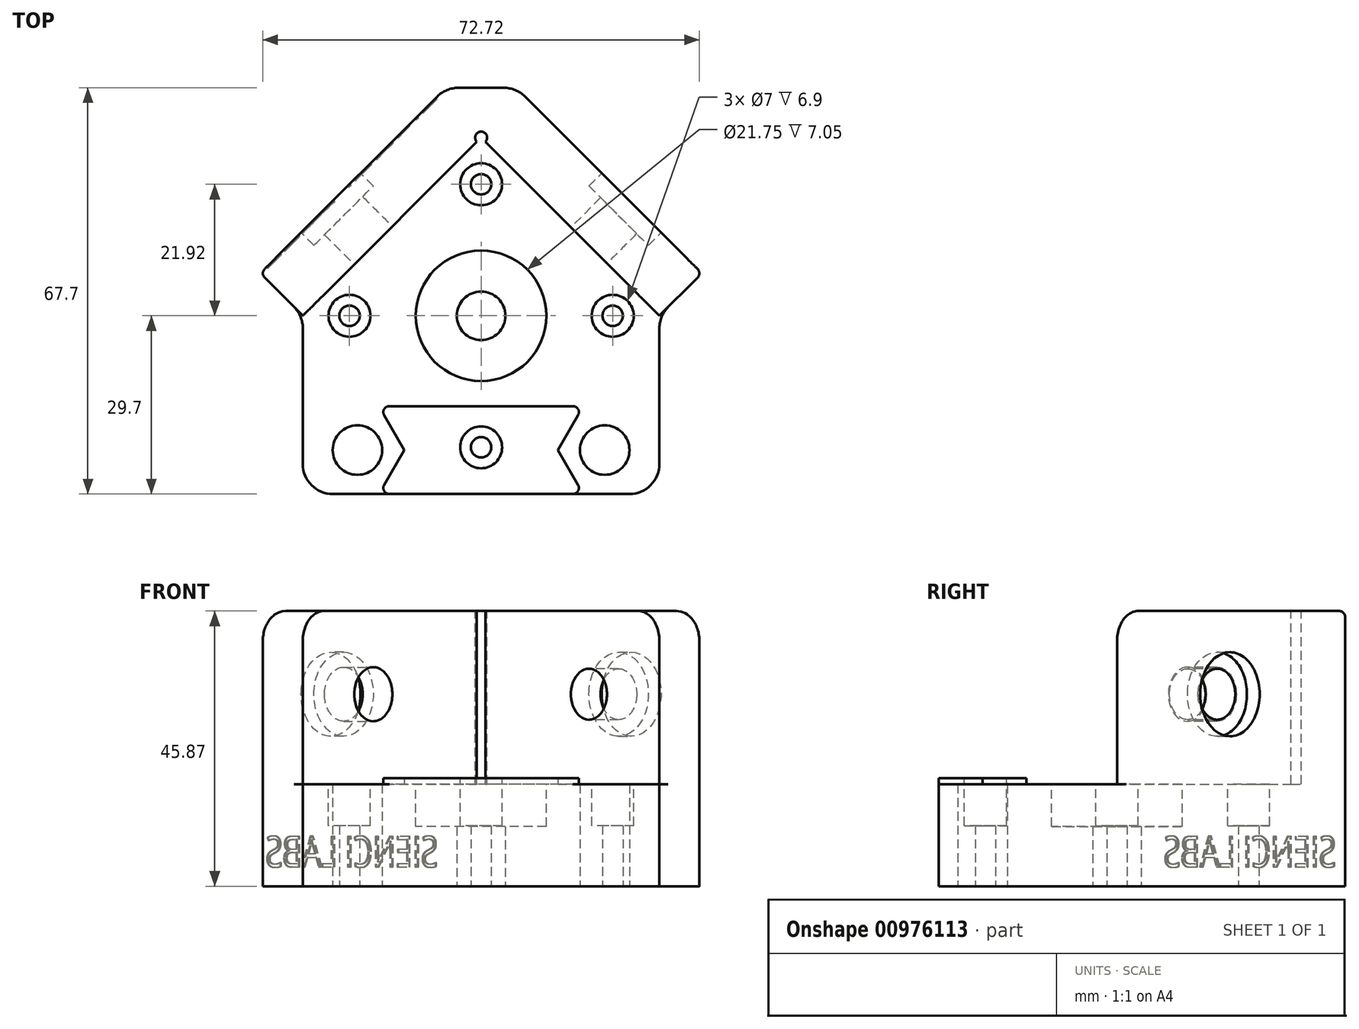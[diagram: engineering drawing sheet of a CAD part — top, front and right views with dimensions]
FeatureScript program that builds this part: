
annotation { "Feature Type Name" : "Feature", "Feature Type Description" : "" }
export const myFeature = defineFeature(function(context is Context, id is Id, definition is map)
    precondition{}
    {
        {
            var Q0;
            Q0=qCreatedBy(makeId("Top.planeOp"),FACE);
            var sketch = newSketch(context, id + "F0", { "sketchPlane" : qUnion([Q0])});
            skLineSegment(sketch, "E0", {"start": v(0, 0) * mm, "end": v(-29.7, 0) * mm});
            skLineSegment(sketch, "E1", {"start": v(-29.7, 0) * mm, "end": v(-29.7, 29.7) * mm});
            skLineSegment(sketch, "E2", {"start": v(-29.7, 29.7) * mm, "end": v(0, 59.4) * mm});
            skLineSegment(sketch, "E3", {"start": v(0, 59.4) * mm, "end": v(0, 0) * mm, "construction": true});
            skLineSegment(sketch, "E4", {"start": v(-29.7, 7.78) * mm, "end": v(0, 7.78) * mm, "construction": true});
            skCircle(sketch, "E5", {"center": v(0, 29.7) * mm, "radius": 4.05 * mm});
            skLineSegment(sketch, "E6", {"start": v(0, 29.7) * mm, "end": v(0, 59.4) * mm, "construction": true});
            skLineSegment(sketch, "E7", {"start": v(0, 59.4) * mm, "end": v(-29.7, 29.7) * mm, "construction": true});
            skLineSegment(sketch, "E8", {"start": v(-29.7, 29.7) * mm, "end": v(0, 0) * mm, "construction": true});
            skLineSegment(sketch, "E9", {"start": v(0, 51.62) * mm, "end": v(-21.92, 29.7) * mm, "construction": true});
            skLineSegment(sketch, "E10", {"start": v(-21.92, 29.7) * mm, "end": v(0, 7.78) * mm, "construction": true});
            skCircle(sketch, "E11", {"center": v(-20.59, 7.32) * mm, "radius": 4.12 * mm});
            skCircle(sketch, "E12", {"center": v(-21.92, 29.7) * mm, "radius": 1.7 * mm});
            skCircle(sketch, "E13", {"center": v(0, 51.62) * mm, "radius": 1.7 * mm});
            skCircle(sketch, "E14", {"center": v(0, 7.78) * mm, "radius": 1.7 * mm});
            skLineSegment(sketch, "E15.MirrorCS", {"start": v(29.7, 29.7) * mm, "end": v(0, 59.4) * mm});
            skLineSegment(sketch, "E16.MirrorCS", {"start": v(0, 0) * mm, "end": v(29.7, 0) * mm});
            skLineSegment(sketch, "E17.MirrorCS", {"start": v(29.7, 0) * mm, "end": v(29.7, 29.7) * mm});
            skLineSegment(sketch, "E18.MirrorCS", {"start": v(29.7, 7.78) * mm, "end": v(0, 7.78) * mm, "construction": true});
            skCircle(sketch, "E19.MirrorC", {"center": v(21.92, 29.7) * mm, "radius": 1.7 * mm});
            skCircle(sketch, "E20.MirrorC", {"center": v(20.6, 7.32) * mm, "radius": 4.12 * mm});
            skLineSegment(sketch, "E21.MirrorCS", {"start": v(0, 59.4) * mm, "end": v(29.7, 29.7) * mm, "construction": true});
            skLineSegment(sketch, "E22.MirrorCS", {"start": v(0, 51.62) * mm, "end": v(21.92, 29.7) * mm, "construction": true});
            skLineSegment(sketch, "E23.MirrorCS", {"start": v(21.92, 29.7) * mm, "end": v(0, 7.78) * mm, "construction": true});
            skLineSegment(sketch, "E24.MirrorCS", {"start": v(29.7, 29.7) * mm, "end": v(0, 0) * mm, "construction": true});
            skSolve(sketch);
        }
        {
            var Q0;
            Q0=qSketchRegion(id+"F0",true);
            extrude(context, id + "F1", {"entities" : qUnion([Q0]), "depth" : 13 * mm, "offsetDistance" : 25 * mm});
        }
        {
            var Q0;
            Q0=makeQuery(id+"F1.opExtrude","CAP_FACE",FACE,{"disambiguationData":[OSD([sQuery(id+"F0.wireOp",EDGE,"E0"),sQuery(id+"F0.wireOp",EDGE,"E1"),sQuery(id+"F0.wireOp",EDGE,"E2"),sQuery(id+"F0.wireOp",EDGE,"E5"),sQuery(id+"F0.wireOp",EDGE,"E11"),sQuery(id+"F0.wireOp",EDGE,"E12"),sQuery(id+"F0.wireOp",EDGE,"E15.MirrorCS"),sQuery(id+"F0.wireOp",EDGE,"E16.MirrorCS"),sQuery(id+"F0.wireOp",EDGE,"E17.MirrorCS"),sQuery(id+"F0.wireOp",EDGE,"E14"),sQuery(id+"F0.wireOp",EDGE,"E13"),sQuery(id+"F0.wireOp",EDGE,"E19.MirrorC"),sQuery(id+"F0.wireOp",EDGE,"E20.MirrorC")])],"isStart":true});
            var sketch = newSketch(context, id + "F2", { "sketchPlane" : qUnion([Q0])});
            skLineSegment(sketch, "E25", {"start": v(-29.7, -29.7) * mm, "end": v(-36.77, -36.77) * mm});
            skLineSegment(sketch, "E26", {"start": v(-36.77, -36.77) * mm, "end": v(-5.84, -67.7) * mm});
            skLineSegment(sketch, "E27", {"start": v(-5.84, -67.7) * mm, "end": v(0, -67.7) * mm});
            skLineSegment(sketch, "E28", {"start": v(0, -29.7) * mm, "end": v(-4.05, -29.7) * mm, "construction": true});
            skLineSegment(sketch, "E29", {"start": v(0, -67.7) * mm, "end": v(0, -29.7) * mm, "construction": true});
            skLineSegment(sketch, "E30.MirrorCS", {"start": v(0, -29.7) * mm, "end": v(4.05, -29.7) * mm, "construction": true});
            skLineSegment(sketch, "E31.MirrorCS", {"start": v(5.84, -67.7) * mm, "end": v(0, -67.7) * mm});
            skLineSegment(sketch, "E32.MirrorCS", {"start": v(36.77, -36.77) * mm, "end": v(5.84, -67.7) * mm});
            skLineSegment(sketch, "E33.MirrorCS", {"start": v(29.7, -29.7) * mm, "end": v(36.77, -36.77) * mm});
            skLineSegment(sketch, "E34", {"start": v(-29.7, -29.7) * mm, "end": v(0, -59.4) * mm});
            skLineSegment(sketch, "E35", {"start": v(0, -59.4) * mm, "end": v(29.7, -29.7) * mm});
            skSolve(sketch);
        }
        {
            var Q0;
            Q0=qSketchRegion(id+"F2",true);
            var Q1;
            Q1=qSketchRegion(id+"F6",true);
            extrude(context, id + "F3", {"entities" : qUnion([Q0, Q1]), "operationType" : NewBodyOperationType.ADD, "oppositeDirection" : true, "depth" : 45.87 * mm, "offsetDistance" : 25 * mm});
        }
        {
            var Q0;
            Q0=makeQuery(id+"F3.opExtrude","SWEPT_FACE",FACE,{"disambiguationData":[OSD([sQuery(id+"F2.wireOp",EDGE,"E34")])]});
            var sketch = newSketch(context, id + "F4", { "sketchPlane" : qUnion([Q0])});
            skCircle(sketch, "E36", {"center": v(16.6, 32) * mm, "radius": 4.5 * mm});
            skLineSegment(sketch, "E37", {"start": v(42, 13) * mm, "end": v(-8.8, 13) * mm, "construction": true});
            skLineSegment(sketch, "E38", {"start": v(16.6, 13) * mm, "end": v(16.6, 45.87) * mm, "construction": true});
            skSolve(sketch);
        }
        {
            var Q0;
            Q0=qSketchRegion(id+"F4",true);
            extrude(context, id + "F5", {"entities" : qUnion([Q0]), "operationType" : NewBodyOperationType.REMOVE, "endBound" : BoundingType.UP_TO_NEXT, "oppositeDirection" : true, "depth" : 25 * mm, "offsetDistance" : 25 * mm});
        }
        {
            var Q0;
            Q0=makeQuery(id+"F3.opExtrude","SWEPT_FACE",FACE,{"disambiguationData":[OSD([sQuery(id+"F2.wireOp",EDGE,"E35")])]});
            var sketch = newSketch(context, id + "F6", { "sketchPlane" : qUnion([Q0])});
            skLineSegment(sketch, "E39", {"start": v(-42, 13) * mm, "end": v(8.8, 13) * mm, "construction": true});
            skLineSegment(sketch, "E40", {"start": v(-16.6, 13) * mm, "end": v(-16.6, 45.87) * mm, "construction": true});
            skCircle(sketch, "E41", {"center": v(-16.6, 32) * mm, "radius": 4.25 * mm});
            skSolve(sketch);
        }
        {
            var Q0;
            Q0=qSketchRegion(id+"F6",true);
            extrude(context, id + "F7", {"entities" : qUnion([Q0]), "operationType" : NewBodyOperationType.REMOVE, "endBound" : BoundingType.UP_TO_NEXT, "oppositeDirection" : true, "depth" : 25 * mm, "offsetDistance" : 25 * mm});
        }
        {
            var Q0;
            Q0=makeQuery(id+"F3.opExtrude","SWEPT_FACE",FACE,{"disambiguationData":[OSD([sQuery(id+"F2.wireOp",EDGE,"E26")])]});
            var sketch = newSketch(context, id + "F8", { "sketchPlane" : qUnion([Q0])});
            skCircle(sketch, "E42", {"center": v(-16.6, 32) * mm, "radius": 7 * mm});
            skSolve(sketch);
        }
        {
            var Q0;
            Q0=qSketchRegion(id+"F8",true);
            extrude(context, id + "F9", {"entities" : qUnion([Q0]), "operationType" : NewBodyOperationType.REMOVE, "oppositeDirection" : true, "depth" : 3 * mm, "offsetDistance" : 25 * mm});
        }
        {
            var Q0;
            Q0=makeQuery(id+"F3.opExtrude","SWEPT_FACE",FACE,{"disambiguationData":[OSD([sQuery(id+"F2.wireOp",EDGE,"E32.MirrorCS")])]});
            var sketch = newSketch(context, id + "F10", { "sketchPlane" : qUnion([Q0])});
            skCircle(sketch, "E43", {"center": v(16.6, 32) * mm, "radius": 7 * mm});
            skSolve(sketch);
        }
        {
            var Q0;
            Q0=qSketchRegion(id+"F10",true);
            extrude(context, id + "F11", {"entities" : qUnion([Q0]), "operationType" : NewBodyOperationType.REMOVE, "oppositeDirection" : true, "depth" : 3 * mm, "offsetDistance" : 25 * mm});
        }
        {
            var Q0;
            Q0=makeQuery(id+"F1.opExtrude","CAP_FACE",FACE,{"disambiguationData":[OSD([sQuery(id+"F0.wireOp",EDGE,"E0"),sQuery(id+"F0.wireOp",EDGE,"E1"),sQuery(id+"F0.wireOp",EDGE,"E2"),sQuery(id+"F0.wireOp",EDGE,"E5"),sQuery(id+"F0.wireOp",EDGE,"E11"),sQuery(id+"F0.wireOp",EDGE,"E12"),sQuery(id+"F0.wireOp",EDGE,"E15.MirrorCS"),sQuery(id+"F0.wireOp",EDGE,"E16.MirrorCS"),sQuery(id+"F0.wireOp",EDGE,"E17.MirrorCS"),sQuery(id+"F0.wireOp",EDGE,"E14"),sQuery(id+"F0.wireOp",EDGE,"E13"),sQuery(id+"F0.wireOp",EDGE,"E19.MirrorC"),sQuery(id+"F0.wireOp",EDGE,"E20.MirrorC")])],"isStart":false});
            var sketch = newSketch(context, id + "F12", { "sketchPlane" : qUnion([Q0])});
            skCircle(sketch, "E44", {"center": v(0, 51.62) * mm, "radius": 3.5 * mm});
            skCircle(sketch, "E45", {"center": v(-21.92, 29.7) * mm, "radius": 3.5 * mm});
            skCircle(sketch, "E46", {"center": v(21.92, 29.7) * mm, "radius": 3.5 * mm});
            skCircle(sketch, "E47", {"center": v(0, 7.78) * mm, "radius": 3.5 * mm});
            skSolve(sketch);
        }
        {
            var Q0;
            Q0=makeQuery(id+"F3.opExtrude","CAP_EDGE",EDGE,{"disambiguationData":[OSD([sQuery(id+"F2.wireOp",EDGE,"E33.MirrorCS")])],"isStart":false});
            var Q1;
            Q1=makeQuery(id+"F3.opExtrude","CAP_EDGE",EDGE,{"disambiguationData":[OSD([sQuery(id+"F2.wireOp",EDGE,"E25")])],"isStart":false});
            var Q2;
            {var subQ0=sQuery(id+"F0.wireOp",EDGE,"E17.MirrorCS");Q2=makeQuery(id+"F3.boolean.opBoolean","MERGE",EDGE,{"derivedFrom":[makeQuery(id+"F1.opExtrude","SWEPT_EDGE",EDGE,{"disambiguationData":[OSD([sQuery(id+"F0.wireOp",EDGE,"E15.MirrorCS"),subQ0])]}),makeQuery(id+"F3.opExtrude","SWEPT_EDGE",EDGE,{"disambiguationData":[OSD([subQ0,sQuery(id+"F2.wireOp",EDGE,"E33.MirrorCS"),sQuery(id+"F2.wireOp",EDGE,"E35")])]})]});}
            var Q3;
            Q3=makeQuery(id+"F1.opExtrude","SWEPT_EDGE",EDGE,{"disambiguationData":[OSD([sQuery(id+"F0.wireOp",EDGE,"E16.MirrorCS"),sQuery(id+"F0.wireOp",EDGE,"E17.MirrorCS")])]});
            var Q4;
            Q4=makeQuery(id+"F1.opExtrude","SWEPT_EDGE",EDGE,{"disambiguationData":[OSD([sQuery(id+"F0.wireOp",EDGE,"E0"),sQuery(id+"F0.wireOp",EDGE,"E1")])]});
            var Q5;
            {var subQ0=sQuery(id+"F0.wireOp",EDGE,"E1");Q5=makeQuery(id+"F3.boolean.opBoolean","MERGE",EDGE,{"derivedFrom":[makeQuery(id+"F1.opExtrude","SWEPT_EDGE",EDGE,{"disambiguationData":[OSD([subQ0,sQuery(id+"F0.wireOp",EDGE,"E2")])]}),makeQuery(id+"F3.opExtrude","SWEPT_EDGE",EDGE,{"disambiguationData":[OSD([subQ0,sQuery(id+"F2.wireOp",EDGE,"E25"),sQuery(id+"F2.wireOp",EDGE,"E34")])]})]});}
            var Q6;
            Q6=makeQuery(id+"F3.opExtrude","SWEPT_EDGE",EDGE,{"disambiguationData":[OSD([sQuery(id+"F2.wireOp",EDGE,"E26"),sQuery(id+"F2.wireOp",EDGE,"E27")])]});
            var Q7;
            Q7=makeQuery(id+"F3.opExtrude","SWEPT_EDGE",EDGE,{"disambiguationData":[OSD([sQuery(id+"F2.wireOp",EDGE,"E31.MirrorCS"),sQuery(id+"F2.wireOp",EDGE,"E32.MirrorCS")])]});
            fillet(context, id + "F13", {"entities" : qUnion([Q0, Q1, Q2, Q3, Q4, Q5, Q6, Q7]), "radius" : 5 * mm, "tangentPropagation" : true, "allowEdgeOverflow" : false});
        }
        {
            var Q0;
            Q0=qSketchRegion(id+"F12",true);
            extrude(context, id + "F14", {"entities" : qUnion([Q0]), "operationType" : NewBodyOperationType.REMOVE, "oppositeDirection" : true, "depth" : 2.9 * mm, "offsetDistance" : 25 * mm});
        }
        {
            var Q0;
            Q0=makeQuery(id+"F3.opExtrude","SWEPT_FACE",FACE,{"disambiguationData":[OSD([sQuery(id+"F2.wireOp",EDGE,"E26")])]});
            var sketch = newSketch(context, id + "F15", { "sketchPlane" : qUnion([Q0])});
            skText(sketch, "E48", { "text": "SIENCI LABS\n", "fontName": "OpenSans-Regular.ttf"});
            const initialGuessF15  = {"E48": [-0.04167, 0.0032, 1, 0, 0.00516]};
            skSetInitialGuess(sketch, initialGuessF15);
            skSolve(sketch);
        }
        {
            var Q0;
            Q0=qSketchRegion(id+"F15",true);
            extrude(context, id + "F16", {"entities" : qUnion([Q0]), "operationType" : NewBodyOperationType.REMOVE, "oppositeDirection" : true, "depth" : 0.25 * mm, "offsetDistance" : 25 * mm});
        }
        {
            var Q0;
            Q0=makeQuery(id+"F1.opExtrude","CAP_FACE",FACE,{"disambiguationData":[OSD([sQuery(id+"F0.wireOp",EDGE,"E0"),sQuery(id+"F0.wireOp",EDGE,"E1"),sQuery(id+"F0.wireOp",EDGE,"E2"),sQuery(id+"F0.wireOp",EDGE,"E5"),sQuery(id+"F0.wireOp",EDGE,"E11"),sQuery(id+"F0.wireOp",EDGE,"E12"),sQuery(id+"F0.wireOp",EDGE,"E15.MirrorCS"),sQuery(id+"F0.wireOp",EDGE,"E16.MirrorCS"),sQuery(id+"F0.wireOp",EDGE,"E17.MirrorCS"),sQuery(id+"F0.wireOp",EDGE,"E14"),sQuery(id+"F0.wireOp",EDGE,"E13"),sQuery(id+"F0.wireOp",EDGE,"E19.MirrorC"),sQuery(id+"F0.wireOp",EDGE,"E20.MirrorC")])],"isStart":false});
            var sketch = newSketch(context, id + "F17", { "sketchPlane" : qUnion([Q0])});
            skCircle(sketch, "E49.cCircle", {"center": v(-20.59, 7.32) * mm, "radius": 6.75 * mm, "construction": true});
            skLineSegment(sketch, "E49.0", {"start": v(-16.7, 14.07) * mm, "end": v(-12.8, 7.32) * mm});
            skLineSegment(sketch, "E49.1", {"start": v(-12.8, 7.32) * mm, "end": v(-16.7, 0.57) * mm});
            skLineSegment(sketch, "E49.2", {"start": v(-16.7, 0.57) * mm, "end": v(-24.49, 0.57) * mm});
            skLineSegment(sketch, "E49.3", {"start": v(-24.49, 0.57) * mm, "end": v(-28.38, 7.32) * mm});
            skLineSegment(sketch, "E49.4", {"start": v(-28.38, 7.32) * mm, "end": v(-24.49, 14.07) * mm});
            skLineSegment(sketch, "E49.5", {"start": v(-24.49, 14.07) * mm, "end": v(-16.7, 14.07) * mm});
            skPoint(sketch, "E49.0.midPoint", {"position": v(-14.74, 10.7) * mm});
            skLineSegment(sketch, "E50", {"start": v(0, 59.4) * mm, "end": v(0, 0) * mm, "construction": true});
            skLineSegment(sketch, "E51.MirrorCS", {"start": v(24.49, 14.07) * mm, "end": v(16.7, 14.07) * mm});
            skLineSegment(sketch, "E52.MirrorCS", {"start": v(16.7, 14.07) * mm, "end": v(12.8, 7.32) * mm});
            skLineSegment(sketch, "E53.MirrorCS", {"start": v(28.38, 7.32) * mm, "end": v(24.49, 14.07) * mm});
            skCircle(sketch, "E54.MirrorC", {"center": v(20.59, 7.32) * mm, "radius": 6.75 * mm, "construction": true});
            skLineSegment(sketch, "E55.MirrorCS", {"start": v(24.49, 0.57) * mm, "end": v(28.38, 7.32) * mm});
            skLineSegment(sketch, "E56.MirrorCS", {"start": v(12.8, 7.32) * mm, "end": v(16.7, 0.57) * mm});
            skLineSegment(sketch, "E57.MirrorCS", {"start": v(16.7, 0.57) * mm, "end": v(24.49, 0.57) * mm});
            skPoint(sketch, "E58.MirrorP", {"position": v(14.74, 10.7) * mm});
            skLineSegment(sketch, "E59", {"start": v(-16.7, 14.07) * mm, "end": v(16.7, 14.07) * mm});
            skLineSegment(sketch, "E60", {"start": v(-16.7, 0.57) * mm, "end": v(16.7, 0.57) * mm});
            skCircle(sketch, "E61", {"center": v(0, 7.78) * mm, "radius": 3.5 * mm});
            skLineSegment(sketch, "E62", {"start": v(-16.7, 0.57) * mm, "end": v(-17.02, 0) * mm});
            skLineSegment(sketch, "E63", {"start": v(-17.02, 0) * mm, "end": v(0, 0) * mm});
            skLineSegment(sketch, "E64.MirrorCS", {"start": v(16.7, 0.57) * mm, "end": v(17.02, 0) * mm});
            skLineSegment(sketch, "E65.MirrorCS", {"start": v(17.02, 0) * mm, "end": v(0, 0) * mm});
            skLineSegment(sketch, "E66", {"start": v(-12.8, 7.32) * mm, "end": v(12.8, 7.32) * mm, "construction": true});
            skLineSegment(sketch, "E67.MirrorCS", {"start": v(-16.7, 14.07) * mm, "end": v(-17.02, 14.64) * mm});
            skLineSegment(sketch, "E68.MirrorCS", {"start": v(16.7, 14.07) * mm, "end": v(17.02, 14.64) * mm});
            skLineSegment(sketch, "E69.MirrorCS", {"start": v(-17.02, 14.64) * mm, "end": v(0, 14.64) * mm});
            skLineSegment(sketch, "E70.MirrorCS", {"start": v(17.02, 14.64) * mm, "end": v(0, 14.64) * mm});
            skSolve(sketch);
        }
        {
            var Q0;
            Q0=makeQuery(id+"F17.imprint","IMPRINT",FACE,{"disambiguationData":[TD([[makeQuery(id+"F17.imprint","IMPRINT",EDGE,{"derivedFrom":sQuery(id+"F17.wireOp",EDGE,"E49.0")}),1.0]])]});
            var Q1;
            Q1=makeQuery(id+"F17.imprint","IMPRINT",FACE,{"disambiguationData":[TD([[makeQuery(id+"F17.imprint","IMPRINT",EDGE,{"derivedFrom":sQuery(id+"F17.wireOp",EDGE,"E60")}),-1.0]])]});
            var Q2;
            Q2=makeQuery(id+"F17.imprint","IMPRINT",FACE,{"disambiguationData":[TD([[makeQuery(id+"F17.imprint","IMPRINT",EDGE,{"derivedFrom":sQuery(id+"F17.wireOp",EDGE,"E67.MirrorCS")}),-1.0]])]});
            extrude(context, id + "F18", {"entities" : qUnion([Q0, Q1, Q2]), "operationType" : NewBodyOperationType.ADD, "depth" : 5 * mm, "offsetDistance" : 25 * mm});
        }
        {
            var Q0;
            Q0=makeQuery(id+"F3.opExtrude","SWEPT_EDGE",EDGE,{"disambiguationData":[OSD([sQuery(id+"F2.wireOp",EDGE,"E32.MirrorCS"),sQuery(id+"F2.wireOp",EDGE,"E33.MirrorCS")])]});
            var Q1;
            Q1=makeQuery(id+"F18.opExtrude","SWEPT_EDGE",EDGE,{"disambiguationData":[OSD([sQuery(id+"F0.wireOp",EDGE,"E0"),sQuery(id+"F0.wireOp",EDGE,"E16.MirrorCS"),sQuery(id+"F17.wireOp",EDGE,"E62"),sQuery(id+"F17.wireOp",EDGE,"E63")])]});
            var Q2;
            Q2=makeQuery(id+"F18.opExtrude","SWEPT_EDGE",EDGE,{"disambiguationData":[OSD([sQuery(id+"F17.wireOp",EDGE,"E67.MirrorCS"),sQuery(id+"F17.wireOp",EDGE,"E69.MirrorCS")])]});
            var Q3;
            Q3=makeQuery(id+"F18.opExtrude","SWEPT_EDGE",EDGE,{"disambiguationData":[OSD([sQuery(id+"F17.wireOp",EDGE,"E68.MirrorCS"),sQuery(id+"F17.wireOp",EDGE,"E70.MirrorCS")])]});
            var Q4;
            Q4=makeQuery(id+"F18.opExtrude","SWEPT_EDGE",EDGE,{"disambiguationData":[OSD([sQuery(id+"F0.wireOp",EDGE,"E0"),sQuery(id+"F0.wireOp",EDGE,"E16.MirrorCS"),sQuery(id+"F17.wireOp",EDGE,"E64.MirrorCS"),sQuery(id+"F17.wireOp",EDGE,"E65.MirrorCS")])]});
            fillet(context, id + "F19", {"entities" : qUnion([Q0, Q1, Q2, Q3, Q4]), "radius" : 1 * mm, "tangentPropagation" : true, "allowEdgeOverflow" : false});
        }
        {
            var Q0;
            Q0=makeQuery(id+"F3.opExtrude","CAP_FACE",FACE,{"disambiguationData":[OSD([sQuery(id+"F2.wireOp",EDGE,"E25"),sQuery(id+"F2.wireOp",EDGE,"E26"),sQuery(id+"F2.wireOp",EDGE,"E27"),sQuery(id+"F2.wireOp",EDGE,"E31.MirrorCS"),sQuery(id+"F2.wireOp",EDGE,"E32.MirrorCS"),sQuery(id+"F2.wireOp",EDGE,"E33.MirrorCS"),sQuery(id+"F2.wireOp",EDGE,"E34"),sQuery(id+"F2.wireOp",EDGE,"E35")])],"isStart":false});
            var sketch = newSketch(context, id + "F20", { "sketchPlane" : qUnion([Q0])});
            skCircle(sketch, "E71", {"center": v(0, 59.4) * mm, "radius": 1 * mm});
            skSolve(sketch);
        }
        {
            var Q0;
            Q0=qSketchRegion(id+"F20",true);
            var Q1;
            Q1=makeQuery(id+"F1.opExtrude","CAP_FACE",FACE,{"disambiguationData":[OSD([sQuery(id+"F0.wireOp",EDGE,"E0"),sQuery(id+"F0.wireOp",EDGE,"E1"),sQuery(id+"F0.wireOp",EDGE,"E2"),sQuery(id+"F0.wireOp",EDGE,"E5"),sQuery(id+"F0.wireOp",EDGE,"E11"),sQuery(id+"F0.wireOp",EDGE,"E12"),sQuery(id+"F0.wireOp",EDGE,"E15.MirrorCS"),sQuery(id+"F0.wireOp",EDGE,"E16.MirrorCS"),sQuery(id+"F0.wireOp",EDGE,"E17.MirrorCS"),sQuery(id+"F0.wireOp",EDGE,"E14"),sQuery(id+"F0.wireOp",EDGE,"E13"),sQuery(id+"F0.wireOp",EDGE,"E19.MirrorC"),sQuery(id+"F0.wireOp",EDGE,"E20.MirrorC")])],"isStart":false});
            extrude(context, id + "F21", {"entities" : qUnion([Q0]), "operationType" : NewBodyOperationType.REMOVE, "endBound" : BoundingType.UP_TO_SURFACE, "oppositeDirection" : true, "depth" : 25 * mm, "endBoundEntityFace" : qUnion([Q1]), "offsetDistance" : 25 * mm});
        }
        {
            var Q0;
            {var subQ0=sQuery(id+"F0.wireOp",EDGE,"E20.MirrorC");var subQ1=sQuery(id+"F0.wireOp",EDGE,"E19.MirrorC");var subQ2=sQuery(id+"F0.wireOp",EDGE,"E13");var subQ3=sQuery(id+"F0.wireOp",EDGE,"E14");var subQ4=sQuery(id+"F0.wireOp",EDGE,"E17.MirrorCS");var subQ5=sQuery(id+"F0.wireOp",EDGE,"E16.MirrorCS");var subQ6=sQuery(id+"F0.wireOp",EDGE,"E15.MirrorCS");var subQ7=sQuery(id+"F0.wireOp",EDGE,"E12");var subQ8=sQuery(id+"F0.wireOp",EDGE,"E11");var subQ9=sQuery(id+"F0.wireOp",EDGE,"E5");var subQ10=sQuery(id+"F0.wireOp",EDGE,"E2");var subQ11=sQuery(id+"F0.wireOp",EDGE,"E1");var subQ12=sQuery(id+"F0.wireOp",EDGE,"E0");Q0=makeQuery(id+"F21.boolean.opBoolean","MERGE",FACE,{"derivedFrom":[makeQuery(id+"F1.opExtrude","CAP_FACE",FACE,{"disambiguationData":[OSD([subQ12,subQ11,subQ10,subQ9,subQ8,subQ7,subQ6,subQ5,subQ4,subQ3,subQ2,subQ1,subQ0])],"isStart":false}),makeQuery(id+"F21.opExtrude","CAP_FACE",FACE,{"disambiguationData":[OSD([subQ12,subQ11,subQ10,subQ9,subQ8,subQ7,subQ6,subQ5,subQ4,subQ3,subQ2,subQ1,subQ0])],"isStart":false})]});}
            var sketch = newSketch(context, id + "F22", { "sketchPlane" : qUnion([Q0])});
            skCircle(sketch, "E72", {"center": v(0, 29.7) * mm, "radius": 10.88 * mm});
            skSolve(sketch);
        }
        {
            var Q0;
            {var subQ0=sQuery(id+"F0.wireOp",EDGE,"E20.MirrorC");var subQ1=sQuery(id+"F0.wireOp",EDGE,"E19.MirrorC");var subQ2=sQuery(id+"F0.wireOp",EDGE,"E13");var subQ3=sQuery(id+"F0.wireOp",EDGE,"E14");var subQ4=sQuery(id+"F0.wireOp",EDGE,"E17.MirrorCS");var subQ5=sQuery(id+"F0.wireOp",EDGE,"E16.MirrorCS");var subQ6=sQuery(id+"F0.wireOp",EDGE,"E15.MirrorCS");var subQ7=sQuery(id+"F0.wireOp",EDGE,"E12");var subQ8=sQuery(id+"F0.wireOp",EDGE,"E11");var subQ9=sQuery(id+"F0.wireOp",EDGE,"E5");var subQ10=sQuery(id+"F0.wireOp",EDGE,"E2");var subQ11=sQuery(id+"F0.wireOp",EDGE,"E1");var subQ12=sQuery(id+"F0.wireOp",EDGE,"E0");Q0=makeQuery(id+"F21.boolean.opBoolean","MERGE",FACE,{"derivedFrom":[makeQuery(id+"F1.opExtrude","CAP_FACE",FACE,{"disambiguationData":[OSD([subQ12,subQ11,subQ10,subQ9,subQ8,subQ7,subQ6,subQ5,subQ4,subQ3,subQ2,subQ1,subQ0])],"isStart":false}),makeQuery(id+"F21.opExtrude","CAP_FACE",FACE,{"disambiguationData":[OSD([subQ12,subQ11,subQ10,subQ9,subQ8,subQ7,subQ6,subQ5,subQ4,subQ3,subQ2,subQ1,subQ0])],"isStart":false})]});}
            var sketch = newSketch(context, id + "F23", { "sketchPlane" : qUnion([Q0])});
            skLineSegment(sketch, "E73.0.0", {"start": v(29.7, 29.7) * mm, "end": v(0.7, 58.7) * mm});
            skArc(sketch, "E73.0.1", {"start": v(-0.7, 58.7) * mm, "mid": v(0, 60.4) * mm, "end": v(0.7, 58.7) * mm});
            skLineSegment(sketch, "E73.0.2", {"start": v(-0.7, 58.7) * mm, "end": v(-29.7, 29.7) * mm});
            skLineSegment(sketch, "E73.0.3", {"start": v(-29.7, 29.7) * mm, "end": v(-31.16, 31.16) * mm});
            skArc(sketch, "E73.0.4", {"start": v(-31.16, 31.16) * mm, "mid": v(-30.08, 29.54) * mm, "end": v(-29.7, 27.63) * mm});
            skLineSegment(sketch, "E73.0.5", {"start": v(-29.7, 27.63) * mm, "end": v(-29.7, 5) * mm});
            skArc(sketch, "E73.0.6", {"start": v(-29.7, 5) * mm, "mid": v(-28.23, 1.46) * mm, "end": v(-24.7, 0) * mm});
            skLineSegment(sketch, "E73.0.7", {"start": v(-24.7, 0) * mm, "end": v(-15.29, 0) * mm});
            skArc(sketch, "E73.0.8", {"start": v(-15.29, 0) * mm, "mid": v(-16.16, 0.5) * mm, "end": v(-16.16, 1.5) * mm});
            skLineSegment(sketch, "E73.0.9", {"start": v(-16.16, 1.5) * mm, "end": v(-12.8, 7.32) * mm});
            skLineSegment(sketch, "E73.0.10", {"start": v(-12.8, 7.32) * mm, "end": v(-16.16, 13.14) * mm});
            skArc(sketch, "E73.0.11", {"start": v(-16.16, 13.14) * mm, "mid": v(-16.16, 14.14) * mm, "end": v(-15.29, 14.64) * mm});
            skLineSegment(sketch, "E73.0.12", {"start": v(-15.29, 14.64) * mm, "end": v(15.29, 14.64) * mm});
            skArc(sketch, "E73.0.13", {"start": v(15.29, 14.64) * mm, "mid": v(16.16, 14.14) * mm, "end": v(16.16, 13.14) * mm});
            skLineSegment(sketch, "E73.0.14", {"start": v(16.16, 13.14) * mm, "end": v(12.8, 7.32) * mm});
            skLineSegment(sketch, "E73.0.15", {"start": v(12.8, 7.32) * mm, "end": v(16.16, 1.5) * mm});
            skArc(sketch, "E73.0.16", {"start": v(16.16, 1.5) * mm, "mid": v(16.16, 0.5) * mm, "end": v(15.29, 0) * mm});
            skLineSegment(sketch, "E73.0.17", {"start": v(15.29, 0) * mm, "end": v(24.7, 0) * mm});
            skArc(sketch, "E73.0.18", {"start": v(24.7, 0) * mm, "mid": v(28.23, 1.46) * mm, "end": v(29.7, 5) * mm});
            skLineSegment(sketch, "E73.0.19", {"start": v(29.7, 5) * mm, "end": v(29.7, 27.63) * mm});
            skArc(sketch, "E73.0.20", {"start": v(29.7, 27.63) * mm, "mid": v(30.08, 29.54) * mm, "end": v(31.16, 31.16) * mm});
            skLineSegment(sketch, "E73.0.21", {"start": v(31.16, 31.16) * mm, "end": v(29.7, 29.7) * mm});
            skSolve(sketch);
        }
        {
            var Q0;
            Q0 = qSketchRegion(id + "F23", true);
            extrude(context, id + "F24", {"entities" : qUnion([Q0]), "operationType" : NewBodyOperationType.ADD, "depth" : 4 * mm, "offsetDistance" : 25 * mm});
        }
        {
            var Q0;
            Q0=makeQuery(id+"F24.opExtrude","CAP_FACE",FACE,{"disambiguationData":[OSD([sQuery(id+"F23.wireOp",EDGE,"E73.0.0"),sQuery(id+"F23.wireOp",EDGE,"E73.0.1"),sQuery(id+"F23.wireOp",EDGE,"E73.0.2"),sQuery(id+"F23.wireOp",EDGE,"E73.0.3"),sQuery(id+"F23.wireOp",EDGE,"E73.0.4"),sQuery(id+"F23.wireOp",EDGE,"E73.0.5"),sQuery(id+"F23.wireOp",EDGE,"E73.0.6"),sQuery(id+"F23.wireOp",EDGE,"E73.0.7"),sQuery(id+"F23.wireOp",EDGE,"E73.0.8"),sQuery(id+"F23.wireOp",EDGE,"E73.0.9"),sQuery(id+"F23.wireOp",EDGE,"E73.0.10"),sQuery(id+"F23.wireOp",EDGE,"E73.0.11"),sQuery(id+"F23.wireOp",EDGE,"E73.0.12"),sQuery(id+"F23.wireOp",EDGE,"E73.0.13"),sQuery(id+"F23.wireOp",EDGE,"E73.0.14"),sQuery(id+"F23.wireOp",EDGE,"E73.0.15"),sQuery(id+"F23.wireOp",EDGE,"E73.0.16"),sQuery(id+"F23.wireOp",EDGE,"E73.0.17"),sQuery(id+"F23.wireOp",EDGE,"E73.0.18"),sQuery(id+"F23.wireOp",EDGE,"E73.0.19"),sQuery(id+"F23.wireOp",EDGE,"E73.0.20"),sQuery(id+"F23.wireOp",EDGE,"E73.0.21")])],"isStart":false});
            var sketch = newSketch(context, id + "F25", { "sketchPlane" : qUnion([Q0])});
            skCircle(sketch, "E74.0", {"center": v(0, 29.7) * mm, "radius": 10.88 * mm});
            skSolve(sketch);
        }
        {
            var Q0;
            Q0 = qSketchRegion(id + "F25", true);
            extrude(context, id + "F26", {"entities" : qUnion([Q0]), "operationType" : NewBodyOperationType.REMOVE, "oppositeDirection" : true, "depth" : 7.05 * mm, "offsetDistance" : 25 * mm});
        }
        {
            var Q0;
            Q0=makeQuery(id+"F24.opExtrude","CAP_FACE",FACE,{"disambiguationData":[OSD([sQuery(id+"F23.wireOp",EDGE,"E73.0.0"),sQuery(id+"F23.wireOp",EDGE,"E73.0.1"),sQuery(id+"F23.wireOp",EDGE,"E73.0.2"),sQuery(id+"F23.wireOp",EDGE,"E73.0.3"),sQuery(id+"F23.wireOp",EDGE,"E73.0.4"),sQuery(id+"F23.wireOp",EDGE,"E73.0.5"),sQuery(id+"F23.wireOp",EDGE,"E73.0.6"),sQuery(id+"F23.wireOp",EDGE,"E73.0.7"),sQuery(id+"F23.wireOp",EDGE,"E73.0.8"),sQuery(id+"F23.wireOp",EDGE,"E73.0.9"),sQuery(id+"F23.wireOp",EDGE,"E73.0.10"),sQuery(id+"F23.wireOp",EDGE,"E73.0.11"),sQuery(id+"F23.wireOp",EDGE,"E73.0.12"),sQuery(id+"F23.wireOp",EDGE,"E73.0.13"),sQuery(id+"F23.wireOp",EDGE,"E73.0.14"),sQuery(id+"F23.wireOp",EDGE,"E73.0.15"),sQuery(id+"F23.wireOp",EDGE,"E73.0.16"),sQuery(id+"F23.wireOp",EDGE,"E73.0.17"),sQuery(id+"F23.wireOp",EDGE,"E73.0.18"),sQuery(id+"F23.wireOp",EDGE,"E73.0.19"),sQuery(id+"F23.wireOp",EDGE,"E73.0.20"),sQuery(id+"F23.wireOp",EDGE,"E73.0.21")])],"isStart":false});
            var sketch = newSketch(context, id + "F27", { "sketchPlane" : qUnion([Q0])});
            skSolve(sketch);
        }
        {
            var Q0;
            Q0=makeQuery(id+"F27.imprint","IMPRINT",FACE,{"disambiguationData":[TD([[makeQuery(id+"F27.imprint","IMPRINT",EDGE,{"derivedFrom":makeQuery(id+"F24.opExtrude","CAP_EDGE",EDGE,{"disambiguationData":[OSD([sQuery(id+"F23.wireOp",EDGE,"E73.0.4")])],"isStart":false})}),1.0]])]});
            var sketch = newSketch(context, id + "F28", { "sketchPlane" : qUnion([Q0])});
            skSolve(sketch);
        }
        {
            var Q0;
            Q0=makeQuery(id+"F28.imprint","IMPRINT",FACE,{"disambiguationData":[TD([[makeQuery(id+"F28.imprint","IMPRINT",EDGE,{"derivedFrom":makeQuery(id+"F27.imprint","IMPRINT",EDGE,{"derivedFrom":makeQuery(id+"F24.opExtrude","CAP_EDGE",EDGE,{"disambiguationData":[OSD([sQuery(id+"F23.wireOp",EDGE,"E73.0.4")])],"isStart":false})})}),1.0]])]});
            var sketch = newSketch(context, id + "F29", { "sketchPlane" : qUnion([Q0])});
            skCircle(sketch, "E75.0", {"center": v(-20.59, 7.32) * mm, "radius": 4.12 * mm});
            skCircle(sketch, "E76.0", {"center": v(20.6, 7.32) * mm, "radius": 4.12 * mm});
            skCircle(sketch, "E77.0", {"center": v(0, 7.78) * mm, "radius": 1.7 * mm});
            skCircle(sketch, "E78.0", {"center": v(-21.92, 29.7) * mm, "radius": 1.7 * mm});
            skCircle(sketch, "E79.0", {"center": v(0, 51.62) * mm, "radius": 1.7 * mm});
            skCircle(sketch, "E80.0", {"center": v(0, 29.7) * mm, "radius": 4.05 * mm});
            skCircle(sketch, "E81.0", {"center": v(21.92, 29.7) * mm, "radius": 1.7 * mm});
            skSolve(sketch);
        }
        {
            var Q0;
            Q0 = qSketchRegion(id + "F29", true);
            var Q1;
            Q1=makeQuery(id+"F3.boolean.opBoolean","MERGE",FACE,{"derivedFrom":[makeQuery(id+"F1.opExtrude","CAP_FACE",FACE,{"disambiguationData":[OSD([sQuery(id+"F0.wireOp",EDGE,"E0"),sQuery(id+"F0.wireOp",EDGE,"E1"),sQuery(id+"F0.wireOp",EDGE,"E2"),sQuery(id+"F0.wireOp",EDGE,"E5"),sQuery(id+"F0.wireOp",EDGE,"E11"),sQuery(id+"F0.wireOp",EDGE,"E12"),sQuery(id+"F0.wireOp",EDGE,"E15.MirrorCS"),sQuery(id+"F0.wireOp",EDGE,"E16.MirrorCS"),sQuery(id+"F0.wireOp",EDGE,"E17.MirrorCS"),sQuery(id+"F0.wireOp",EDGE,"E14"),sQuery(id+"F0.wireOp",EDGE,"E13"),sQuery(id+"F0.wireOp",EDGE,"E19.MirrorC"),sQuery(id+"F0.wireOp",EDGE,"E20.MirrorC")])],"isStart":true}),makeQuery(id+"F3.opExtrude","CAP_FACE",FACE,{"disambiguationData":[OSD([sQuery(id+"F2.wireOp",EDGE,"E25"),sQuery(id+"F2.wireOp",EDGE,"E26"),sQuery(id+"F2.wireOp",EDGE,"E27"),sQuery(id+"F2.wireOp",EDGE,"E31.MirrorCS"),sQuery(id+"F2.wireOp",EDGE,"E32.MirrorCS"),sQuery(id+"F2.wireOp",EDGE,"E33.MirrorCS"),sQuery(id+"F2.wireOp",EDGE,"E34"),sQuery(id+"F2.wireOp",EDGE,"E35")])],"isStart":true})]});
            extrude(context, id + "F30", {"entities" : qUnion([Q0]), "operationType" : NewBodyOperationType.REMOVE, "endBound" : BoundingType.UP_TO_SURFACE, "oppositeDirection" : true, "depth" : 25 * mm, "endBoundEntityFace" : qUnion([Q1]), "offsetDistance" : 25 * mm});
        }
        {
            var Q0;
            Q0=makeQuery(id+"F28.imprint","IMPRINT",FACE,{"disambiguationData":[TD([[makeQuery(id+"F28.imprint","IMPRINT",EDGE,{"derivedFrom":makeQuery(id+"F27.imprint","IMPRINT",EDGE,{"derivedFrom":makeQuery(id+"F24.opExtrude","CAP_EDGE",EDGE,{"disambiguationData":[OSD([sQuery(id+"F23.wireOp",EDGE,"E73.0.4")])],"isStart":false})})}),1.0]])]});
            var sketch = newSketch(context, id + "F31", { "sketchPlane" : qUnion([Q0])});
            skCircle(sketch, "E82.0", {"center": v(-21.92, 29.7) * mm, "radius": 3.5 * mm});
            skCircle(sketch, "E83.0", {"center": v(21.92, 29.7) * mm, "radius": 3.5 * mm});
            skCircle(sketch, "E84.0", {"center": v(0, 51.62) * mm, "radius": 3.5 * mm});
            skCircle(sketch, "E85.0", {"center": v(0, 7.78) * mm, "radius": 3.5 * mm});
            skSolve(sketch);
        }
        {
            var Q0;
            Q0 = qSketchRegion(id + "F31", true);
            extrude(context, id + "F32", {"entities" : qUnion([Q0]), "operationType" : NewBodyOperationType.REMOVE, "oppositeDirection" : true, "depth" : 5 * mm, "offsetDistance" : 25 * mm});
        }
    });
